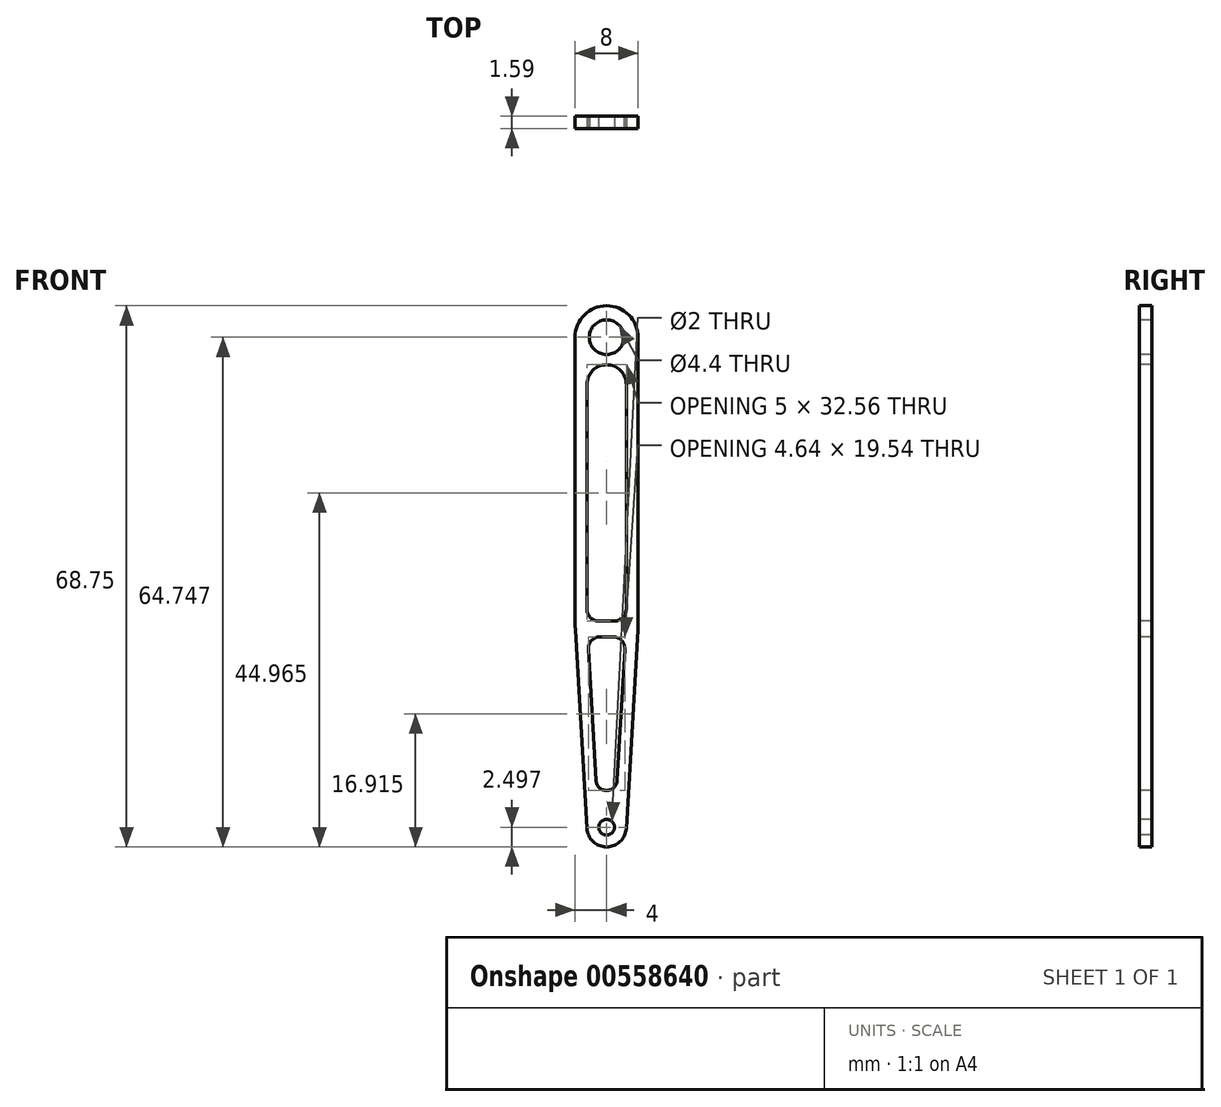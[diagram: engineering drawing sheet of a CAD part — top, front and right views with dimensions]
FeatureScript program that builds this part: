
annotation { "Feature Type Name" : "Feature", "Feature Type Description" : "" }
export const myFeature = defineFeature(function(context is Context, id is Id, definition is map)
    precondition{}
    {
        {
            var Q0;
            Q0=qCreatedBy(makeId("Front.planeOp"),FACE);
            var sketch = newSketch(context, id + "F0", { "sketchPlane" : qUnion([Q0])});
            skLineSegment(sketch, "E0", {"start": v(-4, -6.88) * mm, "end": v(-4, 29.12) * mm});
            skLineSegment(sketch, "E1", {"start": v(4, 29.12) * mm, "end": v(4, -6.88) * mm});
            skArc(sketch, "E2", {"start": v(-4, 29.12) * mm, "mid": v(0, 33.12) * mm, "end": v(4, 29.12) * mm});
            skArc(sketch, "E3", {"start": v(2.5, -33.28) * mm, "mid": v(0, -35.63) * mm, "end": v(-2.5, -33.28) * mm});
            skLineSegment(sketch, "E4", {"start": v(0, 37.08) * mm, "end": v(0, -38.84) * mm, "construction": true});
            skCircle(sketch, "E5", {"center": v(0, 29.12) * mm, "radius": 2.2 * mm});
            skCircle(sketch, "E6", {"center": v(0, -33.13) * mm, "radius": 1 * mm});
            skLineSegment(sketch, "E7", {"start": v(-2.5, 23.12) * mm, "end": v(-2.5, -5.45) * mm});
            skLineSegment(sketch, "E8", {"start": v(-1, -6.95) * mm, "end": v(1, -6.95) * mm});
            skLineSegment(sketch, "E9", {"start": v(2.5, -5.45) * mm, "end": v(2.5, 23.12) * mm});
            skArc(sketch, "E10", {"start": v(-2.5, 23.12) * mm, "mid": v(0, 25.62) * mm, "end": v(2.5, 23.12) * mm});
            skArc(sketch, "E11", {"start": v(-4, -6.88) * mm, "mid": v(-4, -7.47) * mm, "end": v(-3.97, -8.05) * mm});
            skLineSegment(sketch, "E12", {"start": v(-2.5, -33.28) * mm, "end": v(-3.97, -8.05) * mm});
            skArc(sketch, "E13.MirrorCS", {"start": v(4, -6.88) * mm, "mid": v(4, -7.47) * mm, "end": v(3.97, -8.05) * mm});
            skLineSegment(sketch, "E14.MirrorCS", {"start": v(2.5, -33.28) * mm, "end": v(3.97, -8.05) * mm});
            skLineSegment(sketch, "E15", {"start": v(-1.35, -27.21) * mm, "end": v(-2.32, -10.53) * mm});
            skLineSegment(sketch, "E16", {"start": v(-0.82, -8.95) * mm, "end": v(0.82, -8.95) * mm});
            skLineSegment(sketch, "E17", {"start": v(2.32, -10.53) * mm, "end": v(1.35, -27.21) * mm});
            skArc(sketch, "E18", {"start": v(-1.35, -27.21) * mm, "mid": v(0, -28.48) * mm, "end": v(1.35, -27.21) * mm});
            skPoint(sketch, "E19.visualSharp", {"position": v(-2.41, -8.95) * mm});
            skArc(sketch, "E19.filletArc", {"start": v(-0.82, -8.95) * mm, "mid": v(-1.91, -9.42) * mm, "end": v(-2.32, -10.53) * mm});
            skPoint(sketch, "E20.visualSharp", {"position": v(2.41, -8.95) * mm});
            skArc(sketch, "E20.filletArc", {"start": v(2.32, -10.53) * mm, "mid": v(1.91, -9.42) * mm, "end": v(0.82, -8.95) * mm});
            skPoint(sketch, "E21.visualSharp", {"position": v(-2.5, -6.95) * mm});
            skArc(sketch, "E21.filletArc", {"start": v(-2.5, -5.45) * mm, "mid": v(-2.06, -6.5) * mm, "end": v(-1, -6.95) * mm});
            skPoint(sketch, "E22.visualSharp", {"position": v(2.5, -6.95) * mm});
            skArc(sketch, "E22.filletArc", {"start": v(1, -6.95) * mm, "mid": v(2.06, -6.5) * mm, "end": v(2.5, -5.45) * mm});
            skSolve(sketch);
        }
        {
            var Q0;
            Q0 = qSketchRegion(id + "F0", true);
            extrude(context, id + "F1", {"entities" : qUnion([Q0]), "oppositeDirection" : true, "depth" : 1.59 * mm, "offsetDistance" : 25 * mm});
        }
    });
